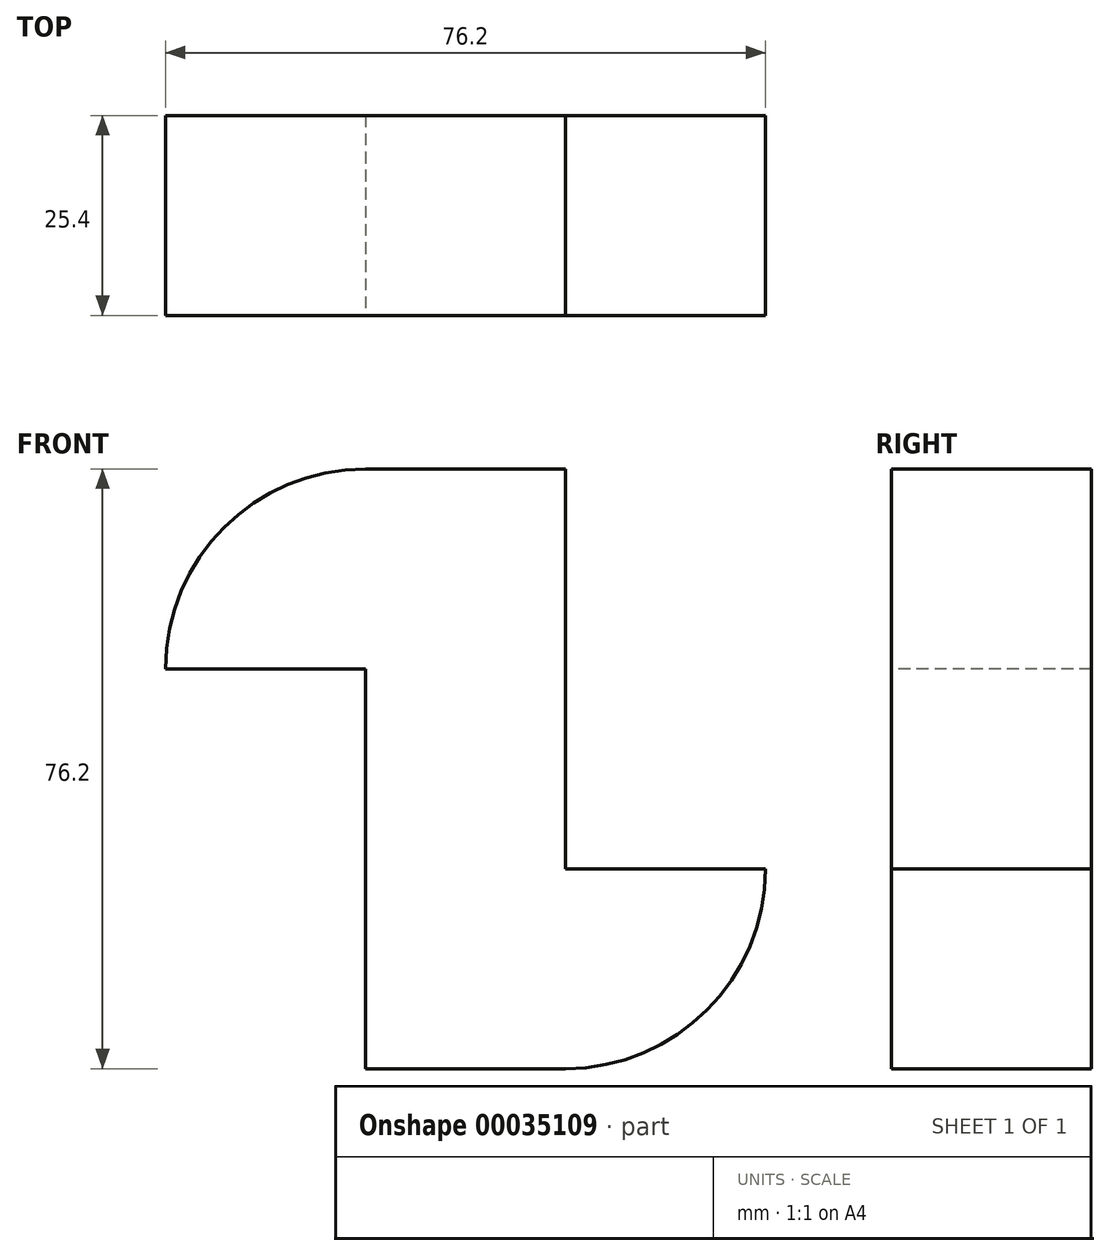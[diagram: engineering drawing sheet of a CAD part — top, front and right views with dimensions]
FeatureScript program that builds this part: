
annotation { "Feature Type Name" : "Feature", "Feature Type Description" : "" }
export const myFeature = defineFeature(function(context is Context, id is Id, definition is map)
    precondition{}
    {
        {
            var Q0;
            Q0=qCreatedBy(makeId("Top.planeOp"),FACE);
            var sketch = newSketch(context, id + "F0", { "sketchPlane" : qUnion([Q0])});
            skLineSegment(sketch, "E0", {"start": v(0, 0) * mm, "end": v(0, 25.4) * mm});
            skLineSegment(sketch, "E1", {"start": v(0, 25.4) * mm, "end": v(50.8, 25.4) * mm});
            skLineSegment(sketch, "E2", {"start": v(50.8, 25.4) * mm, "end": v(50.8, 0) * mm});
            skLineSegment(sketch, "E3", {"start": v(50.8, 0) * mm, "end": v(0, 0) * mm});
            skSolve(sketch);
        }
        {
            var Q0;
            Q0=makeQuery(id+"F0.imprint","IMPRINT",FACE,{"disambiguationData":[TD([[makeQuery(id+"F0.imprint","IMPRINT",EDGE,{"derivedFrom":sQuery(id+"F0.wireOp",EDGE,"E0")}),-1.0]])]});
            extrude(context, id + "F1", {"entities" : qUnion([Q0]), "depth" : 25.4 * mm});
        }
        {
            var Q0;
            Q0=makeQuery(id+"F1.opExtrude","CAP_FACE",FACE,{"disambiguationData":[OSD([sQuery(id+"F0.wireOp",EDGE,"E0"),sQuery(id+"F0.wireOp",EDGE,"E1"),sQuery(id+"F0.wireOp",EDGE,"E2"),sQuery(id+"F0.wireOp",EDGE,"E3")])],"isStart":false});
            var sketch = newSketch(context, id + "F2", { "sketchPlane" : qUnion([Q0])});
            skLineSegment(sketch, "E4", {"start": v(0, 0) * mm, "end": v(0, 25.4) * mm});
            skLineSegment(sketch, "E5", {"start": v(0, 25.4) * mm, "end": v(25.4, 25.4) * mm});
            skLineSegment(sketch, "E6", {"start": v(25.4, 25.4) * mm, "end": v(25.4, 0) * mm});
            skLineSegment(sketch, "E7", {"start": v(25.4, 0) * mm, "end": v(0, 0) * mm});
            skSolve(sketch);
        }
        {
            var Q0;
            Q0=makeQuery(id+"F2.imprint","IMPRINT",FACE,{"disambiguationData":[TD([[makeQuery(id+"F2.imprint","IMPRINT",EDGE,{"derivedFrom":sQuery(id+"F2.wireOp",EDGE,"E4")}),-1.0]])]});
            extrude(context, id + "F3", {"entities" : qUnion([Q0]), "operationType" : NewBodyOperationType.ADD, "depth" : 50.8 * mm});
        }
        {
            var Q0;
            Q0=makeQuery(id+"F3.boolean.opBoolean","MERGE",FACE,{"derivedFrom":[makeQuery(id+"F1.opExtrude","SWEPT_FACE",FACE,{"disambiguationData":[OSD([sQuery(id+"F0.wireOp",EDGE,"E0")])]}),makeQuery(id+"F3.opExtrude","SWEPT_FACE",FACE,{"disambiguationData":[OSD([sQuery(id+"F2.wireOp",EDGE,"E4")])]})]});
            var sketch = newSketch(context, id + "F4", { "sketchPlane" : qUnion([Q0])});
            skLineSegment(sketch, "E8", {"start": v(-25.4, 76.2) * mm, "end": v(-25.4, 50.8) * mm});
            skLineSegment(sketch, "E9", {"start": v(-25.4, 50.8) * mm, "end": v(0, 50.8) * mm});
            skLineSegment(sketch, "E10", {"start": v(0, 50.8) * mm, "end": v(0, 76.2) * mm});
            skLineSegment(sketch, "E11", {"start": v(0, 76.2) * mm, "end": v(-25.4, 76.2) * mm});
            skSolve(sketch);
        }
        {
            var Q0;
            Q0=makeQuery(id+"F4.imprint","IMPRINT",FACE,{"disambiguationData":[TD([[makeQuery(id+"F4.imprint","IMPRINT",EDGE,{"derivedFrom":sQuery(id+"F4.wireOp",EDGE,"E8")}),1.0]])]});
            extrude(context, id + "F5", {"entities" : qUnion([Q0]), "operationType" : NewBodyOperationType.ADD, "depth" : 25.4 * mm});
        }
        {
            var Q0;
            Q0=makeQuery(id+"F1.opExtrude","CAP_EDGE",EDGE,{"disambiguationData":[OSD([sQuery(id+"F0.wireOp",EDGE,"E2")])],"isStart":true});
            var Q1;
            Q1=makeQuery(id+"F5.opExtrude","CAP_EDGE",EDGE,{"disambiguationData":[OSD([sQuery(id+"F4.wireOp",EDGE,"E11")])],"isStart":false});
            fillet(context, id + "F6", {"entities" : qUnion([Q0, Q1]), "radius" : 25.4 * mm, "tangentPropagation" : true, "allowEdgeOverflow" : false});
        }
    });
